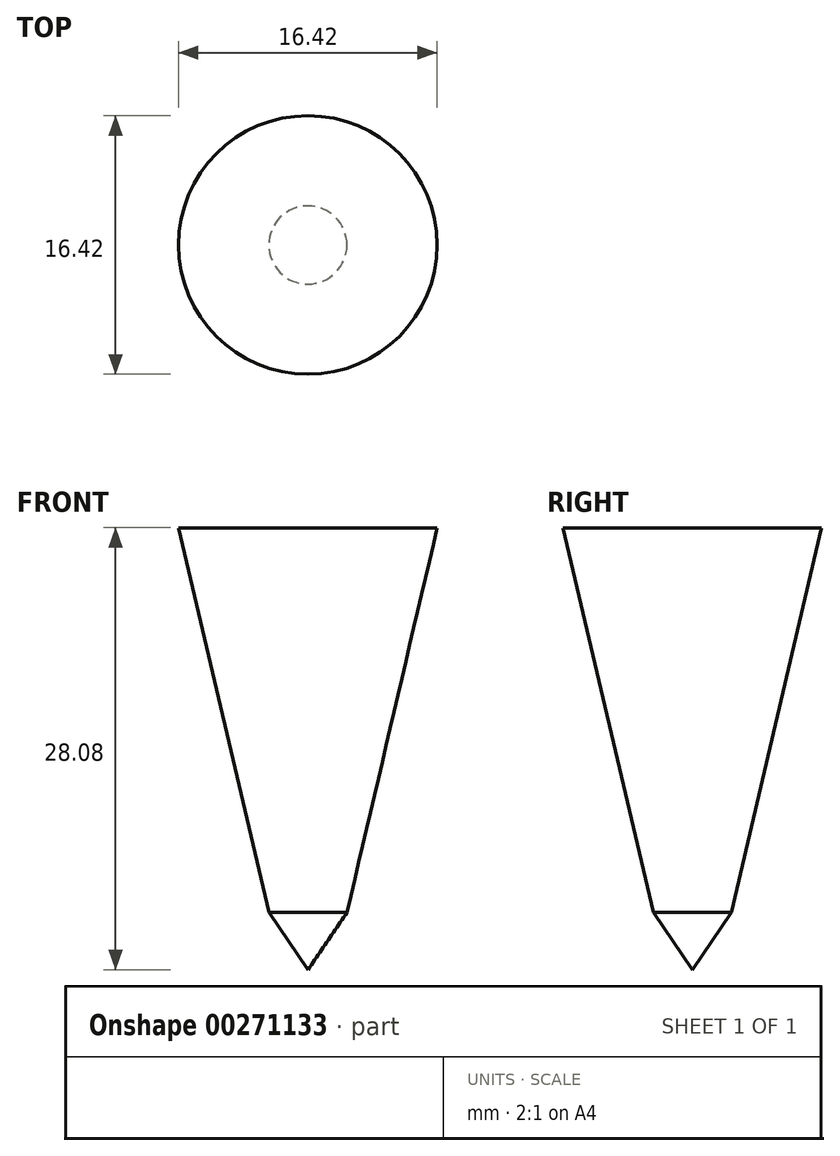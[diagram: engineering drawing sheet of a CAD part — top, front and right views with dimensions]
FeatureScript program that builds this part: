
annotation { "Feature Type Name" : "Feature", "Feature Type Description" : "" }
export const myFeature = defineFeature(function(context is Context, id is Id, definition is map)
    precondition{}
    {
        {
            var Q0;
            Q0=qCreatedBy(makeId("Front.planeOp"),FACE);
            var sketch = newSketch(context, id + "F0", { "sketchPlane" : qUnion([Q0])});
            skLineSegment(sketch, "E0", {"start": v(-42.01, 20.62) * mm, "end": v(-47.74, 45.07) * mm});
            skLineSegment(sketch, "E1", {"start": v(-47.74, 45.07) * mm, "end": v(-39.53, 45.07) * mm});
            skLineSegment(sketch, "E2", {"start": v(-39.53, 45.07) * mm, "end": v(-39.53, 17) * mm});
            skLineSegment(sketch, "E3", {"start": v(-39.53, 17) * mm, "end": v(-42.01, 20.62) * mm});
            skSolve(sketch);
        }
        {
            var Q0;
            Q0 = qSketchRegion(id + "F0", true);
            var Q1;
            Q1=sQuery(id+"F0.wireOp",EDGE,"E2");
            revolve(context, id + "F1", {"entities" : qUnion([Q0]), "axis" : qUnion([Q1]), "revolveType" : RevolveType.FULL});
        }
    });
